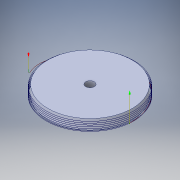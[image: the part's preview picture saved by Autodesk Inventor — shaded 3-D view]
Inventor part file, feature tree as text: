
AUTODESK INVENTOR PART (.ipt)
format: ipt  version: 2016 (Build 200138000, 138)  size: 170,496 bytes
history: native  units: in
note: dims shown in document units (in); Inventor stores cm internally (conversion verified against a paired STEP export)
features: sketch x1, other x1
ambient origin geometry x8: Origin, YZ Plane, XZ Plane, XY Plane, X Axis, Y Axis, Z Axis, Center Point
bodies: Solid1 (feature_tree)
feature tree (2):
  sketch  "Sketch1"
  other  "Boss-Extrude1"
